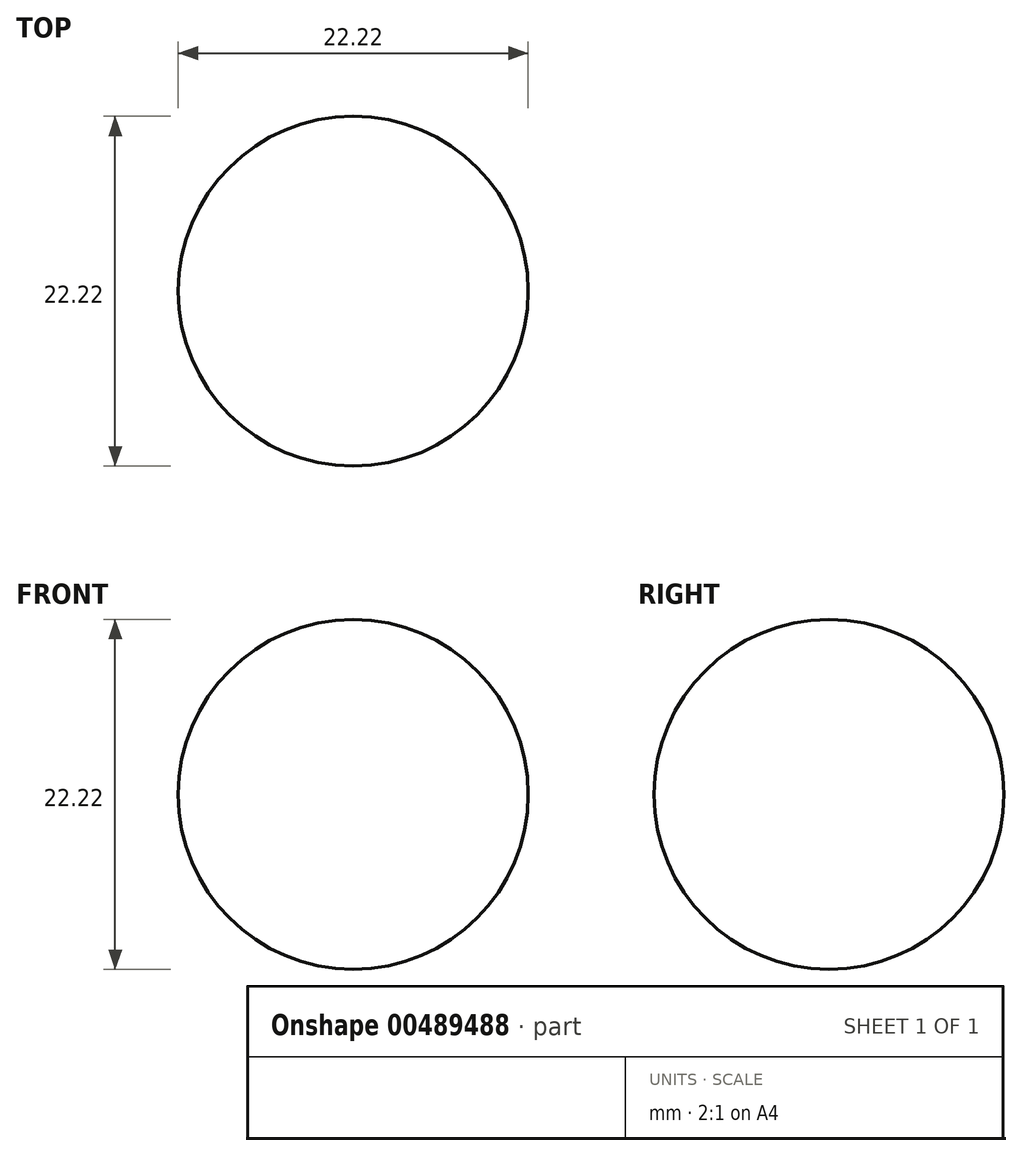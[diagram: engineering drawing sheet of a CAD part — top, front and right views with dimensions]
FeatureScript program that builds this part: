
annotation { "Feature Type Name" : "Feature", "Feature Type Description" : "" }
export const myFeature = defineFeature(function(context is Context, id is Id, definition is map)
    precondition{}
    {
        {
            var Q0;
            Q0=qCreatedBy(makeId("Right.planeOp"),FACE);
            var sketch = newSketch(context, id + "F0", { "sketchPlane" : qUnion([Q0])});
            skLineSegment(sketch, "E0", {"start": v(0, 0) * mm, "end": v(25.4, 0) * mm});
            skLineSegment(sketch, "E1", {"start": v(0, 0) * mm, "end": v(0, 25.4) * mm});
            skLineSegment(sketch, "E2", {"start": v(25.4, 25.4) * mm, "end": v(25.4, 0) * mm});
            skLineSegment(sketch, "E3", {"start": v(25.4, 25.4) * mm, "end": v(0, 25.4) * mm});
            skPoint(sketch, "E4.centerSnap0", {"position": v(0, 12.7) * mm});
            skPoint(sketch, "E4.centerSnap1", {"position": v(12.7, 0) * mm});
            skPoint(sketch, "E4.center.orphan", {"position": v(12.7, 12.7) * mm});
            skCircle(sketch, "E5", {"center": v(12.7, 12.7) * mm, "radius": 11.11 * mm});
            skLineSegment(sketch, "E6", {"start": v(12.7, 25.4) * mm, "end": v(12.7, 0) * mm});
            skSolve(sketch);
        }
        {
            var Q0;
            {var subQ0=sQuery(id+"F0.wireOp",EDGE,"E6");var subQ1=sQuery(id+"F0.wireOp",EDGE,"E5");var subQ2=makeQuery(id+"F0.imprint","INTERSECT",VERTEX,{"disambiguationData":[OD(0.0)],"derivedFrom":[subQ1,subQ0]});Q0=makeQuery(id+"F0.imprint","IMPRINT",FACE,{"disambiguationData":[TD([[makeQuery(id+"F0.imprint","IMPRINT",EDGE,{"disambiguationData":[TD([[subQ2,1.0]])],"derivedFrom":subQ1}),1.0]])]});}
            var Q1;
            Q1=sQuery(id+"F0.wireOp",EDGE,"E6");
            revolve(context, id + "F1", {"entities" : qUnion([Q0]), "axis" : qUnion([Q1]), "revolveType" : RevolveType.FULL});
        }
    });
